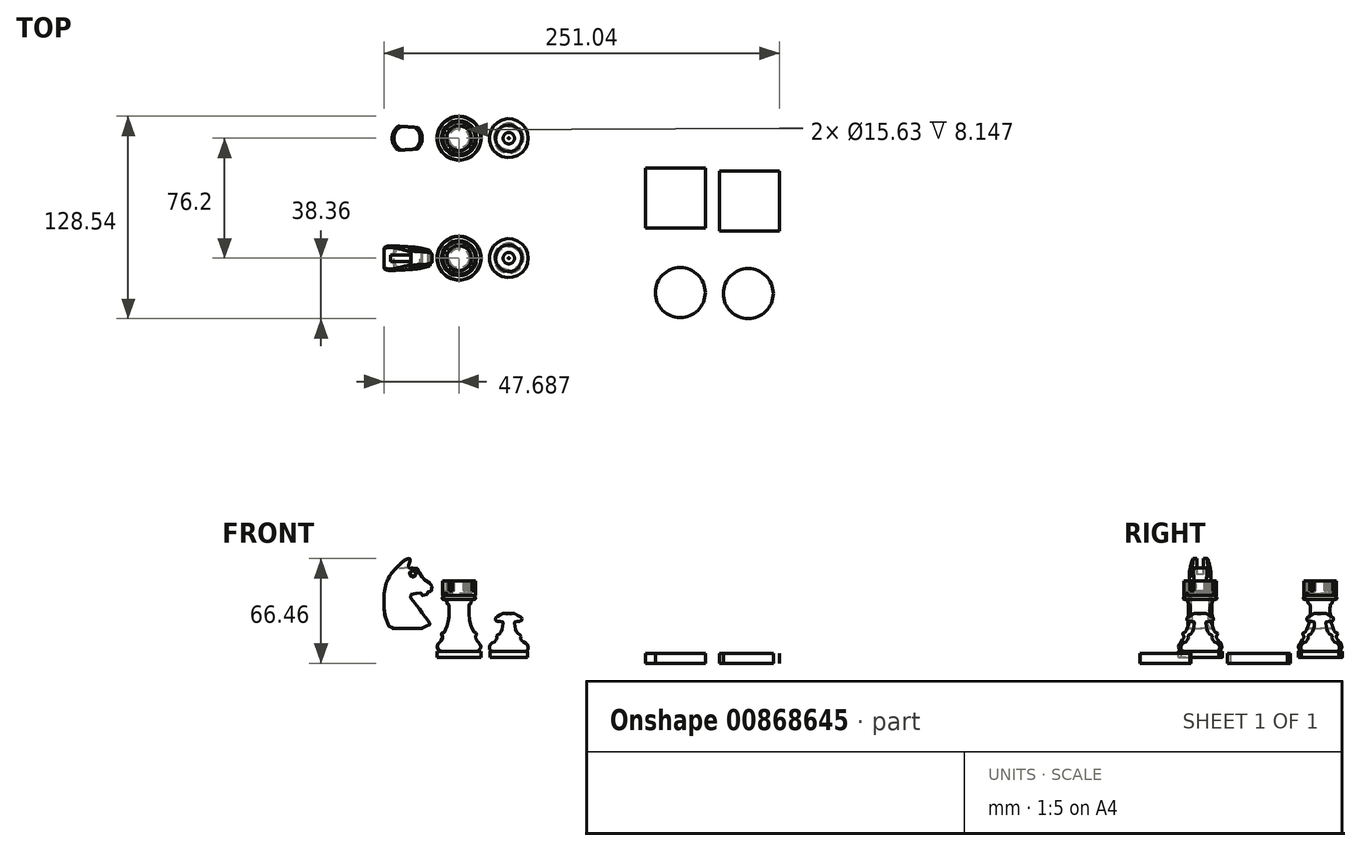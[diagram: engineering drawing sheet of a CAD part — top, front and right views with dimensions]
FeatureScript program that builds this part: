
annotation { "Feature Type Name" : "Feature", "Feature Type Description" : "" }
export const myFeature = defineFeature(function(context is Context, id is Id, definition is map)
    precondition{}
    {
        {
            var Q0;
            Q0=qCreatedBy(makeId("Front.planeOp"),FACE);
            var sketch = newSketch(context, id + "F0", { "sketchPlane" : qUnion([Q0])});
            skLineSegment(sketch, "E0", {"start": v(-199.85, 3.64) * mm, "end": v(-199.85, 7.41) * mm});
            skLineSegment(sketch, "E1", {"start": v(-183.09, 86.79) * mm, "end": v(-183.09, 3.64) * mm});
            skLineSegment(sketch, "E2", {"start": v(-183.09, 3.64) * mm, "end": v(-199.85, 3.64) * mm});
            skLineSegment(sketch, "E3", {"start": v(-199.85, 7.41) * mm, "end": v(-195.88, 7.41) * mm});
            skPoint(sketch, "E4.4.internal.snap0", {"position": v(-197.87, 7.41) * mm});
            skFitSpline(sketch, "E4", {"points": [v(-195.88, 7.41) * mm, v(-197.87, 8.5) * mm, v(-198.95, 10.23) * mm, v(-198.85, 12.89) * mm, v(-197.87, 14.53) * mm, v(-195.76, 16.55) * mm, v(-194.6, 17.92) * mm, v(-194.17, 19.06) * mm, v(-194.57, 20.66) * mm, v(-195.5, 21.71) * mm, v(-195.83, 22.33) * mm, v(-194.7, 22.77) * mm, v(-193.31, 23.31) * mm, v(-192.26, 24.37) * mm, v(-191.14, 25.8) * mm, v(-190.14, 27.4) * mm, v(-189.44, 29.17) * mm, v(-188.91, 31.11) * mm, v(-188.45, 33.14) * mm, v(-188.36, 34.84) * mm, v(-188.35, 36.72) * mm, v(-188.45, 38.4) * mm, v(-188.53, 39.6) * mm, v(-189, 41) * mm, v(-191.73, 41.08) * mm, v(-193.46, 41.44) * mm, v(-194.71, 42.76) * mm, v(-194.2, 44.5) * mm, v(-192.95, 45.2) * mm, v(-191.37, 45.33) * mm, v(-192.24, 45.83) * mm, v(-191.95, 47.6) * mm, v(-190.17, 47.87) * mm, v(-190.03, 49.22) * mm, v(-191.11, 49.48) * mm, v(-191.39, 50.58) * mm, v(-189.6, 51.19) * mm], "startDerivative": vector(-104.08, 42.72) * mm, "endDerivative": vector(159.54, -26.59) * mm});
            skLineSegment(sketch, "E5", {"start": v(-185.2, 71.42) * mm, "end": v(-188.29, 73.11) * mm});
            skLineSegment(sketch, "E6", {"start": v(-188.29, 73.11) * mm, "end": v(-185.32, 75.1) * mm});
            skLineSegment(sketch, "E7", {"start": v(-185.32, 75.1) * mm, "end": v(-189.6, 75.1) * mm});
            skLineSegment(sketch, "E8", {"start": v(-189.6, 75.1) * mm, "end": v(-189.6, 81.24) * mm});
            skLineSegment(sketch, "E9", {"start": v(-189.6, 81.24) * mm, "end": v(-184.77, 81.24) * mm});
            skFitSpline(sketch, "E10", {"points": [v(-189.6, 51.19) * mm, v(-194.54, 65.85) * mm, v(-192.56, 67.9) * mm, v(-188.33, 68.71) * mm, v(-187.1, 69) * mm, v(-188.31, 70.17) * mm, v(-187.66, 71) * mm, v(-185.2, 71.42) * mm], "startDerivative": vector(-6.3, 14.3) * mm, "endDerivative": vector(19.07, 2.88) * mm});
            skPoint(sketch, "E11.2.internal.snap0", {"position": v(-187.18, 81.24) * mm});
            skPoint(sketch, "E11.3.internal.snap0", {"position": v(-187.18, 81.24) * mm});
            skFitSpline(sketch, "E11", {"points": [v(-184.77, 81.24) * mm, v(-186.5, 82.07) * mm, v(-187.18, 83.38) * mm, v(-187.18, 84.69) * mm, v(-186.15, 85.79) * mm, v(-184.77, 86.55) * mm, v(-183.09, 86.79) * mm], "startDerivative": vector(-10.63, 3.55) * mm, "endDerivative": vector(10.1, 0.69) * mm});
            skLineSegment(sketch, "E12", {"start": v(-162.47, 3.64) * mm, "end": v(-147.45, 3.64) * mm});
            skLineSegment(sketch, "E13", {"start": v(-147.45, 3.64) * mm, "end": v(-147.45, 73.04) * mm});
            skArc(sketch, "E14", {"start": v(-147.45, 73.04) * mm, "mid": v(-151.14, 70.8) * mm, "end": v(-148.43, 67.44) * mm});
            skArc(sketch, "E15", {"start": v(-148.43, 67.44) * mm, "mid": v(-152.95, 65.09) * mm, "end": v(-155.31, 60.57) * mm});
            skLineSegment(sketch, "E16", {"start": v(-162.47, 3.64) * mm, "end": v(-162.47, 7.42) * mm});
            skLineSegment(sketch, "E17", {"start": v(-162.47, 7.42) * mm, "end": v(-158.12, 7.42) * mm});
            skPoint(sketch, "E18.1.internal.snap0", {"position": v(-160.3, 7.42) * mm});
            skPoint(sketch, "E18.4.internal.snap0", {"position": v(-160.3, 7.42) * mm});
            skPoint(sketch, "E18.7.internal.snap0", {"position": v(-160.3, 7.42) * mm});
            skFitSpline(sketch, "E18", {"points": [v(-158.12, 7.42) * mm, v(-160.3, 8.25) * mm, v(-161.95, 10.36) * mm, v(-161.95, 13.37) * mm, v(-160.3, 16.08) * mm, v(-159.02, 17.75) * mm, v(-158.68, 20.43) * mm, v(-160.3, 22.38) * mm, v(-158.12, 23) * mm, v(-155.74, 25.18) * mm, v(-154.18, 28.37) * mm, v(-153.34, 32.28) * mm, v(-153.18, 35.56) * mm, v(-153.3, 38.31) * mm, v(-154.3, 40) * mm, v(-158.12, 40.69) * mm, v(-159.15, 41.5) * mm, v(-158.77, 43.64) * mm, v(-155.8, 44.28) * mm, v(-156.78, 44.74) * mm], "startDerivative": vector(-84.67, 31.47) * mm, "endDerivative": vector(-14.48, 19.3) * mm});
            skFitSpline(sketch, "E19", {"points": [v(-155.8, 44.28) * mm, v(-156.78, 44.74) * mm, v(-156.78, 46.4) * mm, v(-155.31, 46.86) * mm, v(-154.54, 47.02) * mm, v(-154.46, 47.67) * mm, v(-155.31, 48) * mm, v(-155.8, 48.59) * mm, v(-155.31, 49.3) * mm, v(-154.8, 49.4) * mm, v(-154.74, 50.75) * mm, v(-154.96, 53) * mm, v(-155.31, 54.38) * mm, v(-156.58, 56.29) * mm, v(-158.17, 57.83) * mm, v(-159.9, 58.84) * mm, v(-159.55, 60.57) * mm, v(-157.83, 61.78) * mm, v(-157.79, 60.57) * mm, v(-156.78, 59.8) * mm, v(-155.31, 60.57) * mm], "startDerivative": vector(25.67, -12.83) * mm, "endDerivative": vector(13.36, 18.62) * mm});
            skLineSegment(sketch, "E20", {"start": v(-113.8, 67.45) * mm, "end": v(-113.8, 3.64) * mm});
            skLineSegment(sketch, "E21", {"start": v(-113.8, 3.64) * mm, "end": v(-127.93, 3.64) * mm});
            skLineSegment(sketch, "E22", {"start": v(-127.93, 3.64) * mm, "end": v(-127.93, 7.42) * mm});
            skLineSegment(sketch, "E23", {"start": v(-127.93, 7.42) * mm, "end": v(-124.73, 7.42) * mm});
            skLineSegment(sketch, "E24", {"start": v(-203.2, 3.64) * mm, "end": v(0.2, 3.64) * mm, "construction": true});
            skLineSegment(sketch, "E25", {"start": v(-0.21, 7.42) * mm, "end": v(-203.2, 7.42) * mm, "construction": true});
            skPoint(sketch, "E26.orphan", {"position": v(-164.6, 7.42) * mm});
            skFitSpline(sketch, "E27", {"points": [v(-124.73, 7.42) * mm, v(-126, 7.93) * mm, v(-127.06, 8.77) * mm, v(-127.82, 10.15) * mm, v(-127.96, 11.35) * mm, v(-127.51, 12.72) * mm, v(-126.8, 13.65) * mm, v(-125.88, 14.3) * mm, v(-124.95, 14.88) * mm, v(-124.14, 15.63) * mm, v(-123.67, 16.5) * mm, v(-123.67, 17.98) * mm, v(-124.73, 19.52) * mm, v(-123.1, 20.19) * mm, v(-121.55, 21.43) * mm, v(-120.23, 23.7) * mm, v(-119.36, 25.7) * mm, v(-118.68, 28.19) * mm, v(-118.44, 30.53) * mm, v(-118.68, 33.54) * mm, v(-120.4, 33.98) * mm, v(-122.54, 34.42) * mm, v(-124, 35.4) * mm, v(-124.17, 36.4) * mm, v(-123.83, 37.34) * mm, v(-122.39, 38.09) * mm, v(-120.99, 38.5) * mm, v(-121.51, 39.23) * mm, v(-121.67, 40.1) * mm, v(-120.93, 40.57) * mm, v(-120.07, 40.83) * mm, v(-119.28, 41.3) * mm, v(-119.17, 42.67) * mm, v(-119.8, 43.04) * mm, v(-120.12, 43.62) * mm, v(-119.67, 44.06) * mm, v(-119.36, 44.12) * mm, v(-120.86, 45.59) * mm, v(-122.01, 47.27) * mm, v(-122.54, 48.85) * mm, v(-122.96, 50.74) * mm, v(-122.75, 52.74) * mm, v(-121.96, 55.36) * mm, v(-120.54, 57.83) * mm, v(-119.28, 59.3) * mm, v(-117.86, 60.62) * mm, v(-115.55, 62.25) * mm], "startDerivative": vector(-65.25, 19.9) * mm, "endDerivative": vector(68.19, 36.9) * mm});
            skArc(sketch, "E28", {"start": v(-113.8, 67.45) * mm, "mid": v(-116.75, 65.54) * mm, "end": v(-115.55, 62.25) * mm});
            skLineSegment(sketch, "E29", {"start": v(-108.32, 59.77) * mm, "end": v(-112.78, 53.82) * mm});
            skLineSegment(sketch, "E30", {"start": v(-112.78, 53.82) * mm, "end": v(-111.45, 52.82) * mm});
            skLineSegment(sketch, "E31", {"start": v(-111.45, 52.82) * mm, "end": v(-107.21, 58.47) * mm});
            skArc(sketch, "E32", {"start": v(-107.21, 58.47) * mm, "mid": v(-106.96, 59.81) * mm, "end": v(-108.32, 59.77) * mm});
            skLineSegment(sketch, "E33", {"start": v(-81.1, 22.23) * mm, "end": v(-81.1, 3.64) * mm});
            skLineSegment(sketch, "E34", {"start": v(-81.1, 3.64) * mm, "end": v(-94.38, 3.64) * mm});
            skLineSegment(sketch, "E35", {"start": v(-94.38, 3.64) * mm, "end": v(-94.38, 7.42) * mm});
            skLineSegment(sketch, "E36", {"start": v(-94.38, 7.42) * mm, "end": v(-90.56, 7.42) * mm});
            skFitSpline(sketch, "E37", {"points": [v(-90.56, 7.42) * mm, v(-92.55, 8.07) * mm, v(-93.98, 9.16) * mm, v(-94.56, 10.65) * mm, v(-94.5, 12.37) * mm, v(-93.76, 13.69) * mm, v(-92.27, 15) * mm, v(-91.12, 16.04) * mm, v(-89.92, 17.64) * mm, v(-89.74, 19.07) * mm, v(-90.56, 20.16) * mm, v(-91.58, 20.97) * mm, v(-91.7, 21.54) * mm, v(-90.56, 22.11) * mm, v(-89.46, 22.23) * mm], "startDerivative": vector(-24.3, 6.47) * mm, "endDerivative": vector(16.76, 0.42) * mm});
            skLineSegment(sketch, "E38", {"start": v(-89.46, 22.23) * mm, "end": v(-81.1, 22.23) * mm});
            skLineSegment(sketch, "E39", {"start": v(-81.1, 22.23) * mm, "end": v(-72, 22.23) * mm});
            skFitSpline(sketch, "E40", {"points": [v(-89.46, 22.23) * mm, v(-91.2, 22.91) * mm, v(-92.34, 23.3) * mm, v(-93.93, 26.73) * mm, v(-95.27, 31.07) * mm, v(-95.78, 40.69) * mm, v(-95.08, 48.01) * mm, v(-92.6, 54.7) * mm, v(-87.82, 60.76) * mm, v(-83.04, 65.15) * mm, v(-80.42, 66.43) * mm, v(-79.15, 66.1) * mm, v(-79.66, 63.5) * mm, v(-80.17, 60.82) * mm, v(-77.62, 60.46) * mm, v(-74.88, 60.37) * mm, v(-73.73, 58.4) * mm, v(-71.82, 55.02) * mm, v(-67.17, 51) * mm, v(-65.58, 50.05) * mm, v(-65.64, 46.42) * mm, v(-66.22, 45.53) * mm, v(-67.62, 46.04) * mm, v(-68.06, 45.97) * mm, v(-68.02, 45.56) * mm, v(-67.03, 45.16) * mm, v(-68.33, 43.99) * mm, v(-69.6, 43.13) * mm, v(-72.16, 43.4) * mm, v(-71.53, 44.4) * mm, v(-72.93, 44.62) * mm, v(-76, 44.21) * mm, v(-78.42, 43.72) * mm, v(-79.19, 43.63) * mm, v(-79.5, 42.68) * mm, v(-78.15, 40.74) * mm, v(-73.83, 35.2) * mm, v(-67.16, 26.15) * mm, v(-66.48, 24.84) * mm, v(-67.2, 24.2) * mm, v(-72, 22.23) * mm], "startDerivative": vector(-89.03, 42.06) * mm, "endDerivative": vector(-168.6, -65.06) * mm});
            skLineSegment(sketch, "E41", {"start": v(-48.1, 44.33) * mm, "end": v(-48.1, 3.64) * mm});
            skLineSegment(sketch, "E42", {"start": v(-48.1, 3.64) * mm, "end": v(-62.08, 3.64) * mm});
            skLineSegment(sketch, "E43", {"start": v(-62.08, 3.64) * mm, "end": v(-62.08, 7.42) * mm});
            skLineSegment(sketch, "E44", {"start": v(-62.08, 7.42) * mm, "end": v(-58.5, 7.42) * mm});
            skFitSpline(sketch, "E45", {"points": [v(-58.5, 7.42) * mm, v(-60.07, 7.9) * mm, v(-61.28, 8.85) * mm, v(-61.91, 10.22) * mm, v(-61.65, 11.69) * mm, v(-60.39, 13.37) * mm, v(-59.02, 15.05) * mm, v(-58.5, 16.84) * mm, v(-59.02, 18.26) * mm, v(-59.28, 18.94) * mm, v(-58.5, 19.41) * mm, v(-57.4, 20) * mm, v(-55.87, 23.62) * mm, v(-54.66, 28.14) * mm, v(-54.45, 36.13) * mm, v(-54.7, 37.6) * mm, v(-55.18, 37.7) * mm, v(-55.81, 38.12) * mm, v(-55.81, 39.07) * mm, v(-56.55, 40.07) * mm, v(-57.23, 40.44) * mm, v(-58.5, 40.65) * mm, v(-58.5, 42.07) * mm, v(-57.4, 42.49) * mm, v(-58.44, 43.17) * mm], "startDerivative": vector(-47.74, 11.1) * mm, "endDerivative": vector(-43.2, 43.2) * mm});
            skLineSegment(sketch, "E46", {"start": v(-58.44, 43.17) * mm, "end": v(-58.44, 52.47) * mm});
            skLineSegment(sketch, "E47", {"start": v(-58.44, 52.47) * mm, "end": v(-55.92, 52.47) * mm});
            skLineSegment(sketch, "E48", {"start": v(-55.92, 52.47) * mm, "end": v(-55.92, 44.33) * mm});
            skLineSegment(sketch, "E49", {"start": v(-55.92, 44.33) * mm, "end": v(-48.1, 44.33) * mm});
            skLineSegment(sketch, "E50", {"start": v(-16.51, 46.86) * mm, "end": v(-16.51, 3.64) * mm});
            skLineSegment(sketch, "E51", {"start": v(-28.54, 3.64) * mm, "end": v(-28.54, 7.42) * mm});
            skLineSegment(sketch, "E52", {"start": v(-28.54, 7.42) * mm, "end": v(-26.05, 7.42) * mm});
            skFitSpline(sketch, "E53", {"points": [v(-26.05, 7.42) * mm, v(-28.06, 8.02) * mm, v(-28.67, 8.98) * mm, v(-28.85, 10.67) * mm, v(-27.88, 12.4) * mm, v(-25.72, 13.71) * mm, v(-24.53, 14.77) * mm, v(-24, 16.37) * mm, v(-24.3, 17.6) * mm, v(-23.06, 18.44) * mm, v(-22, 19.33) * mm, v(-20.8, 21.5) * mm, v(-20.27, 24.06) * mm, v(-20.26, 26.22) * mm, v(-20.94, 26.53) * mm, v(-23.19, 26.71) * mm, v(-24.59, 27) * mm, v(-24.95, 28.67) * mm, v(-23.59, 29.76) * mm, v(-20.12, 31.82) * mm], "startDerivative": vector(-40.56, 0) * mm, "endDerivative": vector(53.61, 36) * mm});
            skArc(sketch, "E54", {"start": v(-16.51, 46.86) * mm, "mid": v(-24.38, 40.8) * mm, "end": v(-20.12, 31.82) * mm});
            skLineSegment(sketch, "E55", {"start": v(-28.54, 3.64) * mm, "end": v(-16.51, 3.64) * mm});
            skLineSegment(sketch, "E56", {"start": v(-185.32, 75.1) * mm, "end": v(-183.09, 75.1) * mm});
            skLineSegment(sketch, "E57", {"start": v(-184.77, 81.24) * mm, "end": v(-183.09, 81.24) * mm});
            skLineSegment(sketch, "E58.MirrorCS", {"start": v(-176.58, 81.24) * mm, "end": v(-181.4, 81.24) * mm});
            skLineSegment(sketch, "E59.MirrorCS", {"start": v(-181.4, 81.24) * mm, "end": v(-183.09, 81.24) * mm});
            skLineSegment(sketch, "E60.MirrorCS", {"start": v(-176.58, 75.1) * mm, "end": v(-176.58, 81.24) * mm});
            skLineSegment(sketch, "E61.MirrorCS", {"start": v(-180.85, 75.1) * mm, "end": v(-176.58, 75.1) * mm});
            skLineSegment(sketch, "E62.MirrorCS", {"start": v(-180.85, 75.1) * mm, "end": v(-183.09, 75.1) * mm});
            skLineSegment(sketch, "E63", {"start": v(-158.15, 61.76) * mm, "end": v(-159.98, 58.99) * mm});
            skFitSpline(sketch, "E64", {"points": [v(-77.62, 60.46) * mm, v(-81.58, 60.46) * mm, v(-86.12, 60.08) * mm, v(-88.95, 59.2) * mm, v(-91.47, 56.45) * mm], "startDerivative": vector(-28.5, -2.2) * mm, "endDerivative": vector(-9.14, -10.07) * mm});
            skArc(sketch, "E65", {"start": v(-78.9, 58.36) * mm, "mid": v(-76.13, 55.42) * mm, "end": v(-78.63, 58.6) * mm});
            skArc(sketch, "E66", {"start": v(-78.58, 58.1) * mm, "mid": v(-76.44, 55.7) * mm, "end": v(-78.35, 58.29) * mm});
            skLineSegment(sketch, "E67", {"start": v(-78.35, 58.29) * mm, "end": v(-78.63, 58.6) * mm});
            skLineSegment(sketch, "E68", {"start": v(-78.58, 58.1) * mm, "end": v(-78.9, 58.36) * mm});
            skSolve(sketch);
        }
        {
            var Q0;
            Q0=makeQuery(id+"F0.imprint","IMPRINT",FACE,{"disambiguationData":[TD([[makeQuery(id+"F0.imprint","IMPRINT",EDGE,{"derivedFrom":sQuery(id+"F0.wireOp",EDGE,"E0")}),-1.0]])]});
            var Q1;
            {var subQ0=sQuery(id+"F0.wireOp",EDGE,"E11");Q1=makeQuery(id+"F0.imprint","IMPRINT",FACE,{"disambiguationData":[TD([[makeQuery(id+"F0.imprint","IMPRINT",EDGE,{"derivedFrom":subQ0}),-1.0]])]});}
            var Q2;
            Q2=sQuery(id+"F0.wireOp",EDGE,"E1");
            revolve(context, id + "F1", {"surfaceOperationType" : NewSurfaceOperationType.NEW, "entities" : qUnion([Q0, Q1]), "axis" : qUnion([Q2]), "revolveType" : RevolveType.FULL});
        }
        {
            var Q0;
            Q0=makeQuery(id+"F0.imprint","IMPRINT",FACE,{"disambiguationData":[TD([[makeQuery(id+"F0.imprint","IMPRINT",EDGE,{"derivedFrom":sQuery(id+"F0.wireOp",EDGE,"E58.MirrorCS")}),1.0]])]});
            var Q1;
            Q1=makeQuery(id+"F0.imprint","IMPRINT",FACE,{"disambiguationData":[TD([[makeQuery(id+"F0.imprint","IMPRINT",EDGE,{"derivedFrom":sQuery(id+"F0.wireOp",EDGE,"E7")}),-1.0]])]});
            extrude(context, id + "F2", {"entities" : qUnion([Q0, Q1]), "endBound" : BoundingType.SYMMETRIC, "depth" : 4.32 * mm, "offsetDistance" : 25.4 * mm});
        }
        {
            var Q0;
            Q0=makeQuery(id+"F0.imprint","IMPRINT",FACE,{"disambiguationData":[TD([[makeQuery(id+"F0.imprint","IMPRINT",EDGE,{"derivedFrom":sQuery(id+"F0.wireOp",EDGE,"E12")}),1.0]])]});
            var Q1;
            {var subQ0=sQuery(id+"F0.wireOp",EDGE,"E63");Q1=makeQuery(id+"F0.imprint","IMPRINT",FACE,{"disambiguationData":[TD([[makeQuery(id+"F0.imprint","IMPRINT",EDGE,{"derivedFrom":subQ0}),-1.0]])]});}
            var Q2;
            Q2=sQuery(id+"F0.wireOp",EDGE,"E13");
            revolve(context, id + "F3", {"surfaceOperationType" : NewSurfaceOperationType.NEW, "entities" : qUnion([Q0, Q1]), "axis" : qUnion([Q2]), "revolveType" : RevolveType.FULL});
        }
        {
            var Q0;
            {var subQ0=sQuery(id+"F0.wireOp",EDGE,"E63");Q0=makeQuery(id+"F0.imprint","IMPRINT",FACE,{"disambiguationData":[TD([[makeQuery(id+"F0.imprint","IMPRINT",EDGE,{"derivedFrom":subQ0}),-1.0]])]});}
            extrude(context, id + "F4", {"entities" : qUnion([Q0]), "operationType" : NewBodyOperationType.REMOVE, "endBound" : BoundingType.SYMMETRIC, "oppositeDirection" : true, "depth" : 7.62 * mm, "offsetDistance" : 25.4 * mm});
        }
        {
            var Q0;
            Q0=makeQuery(id+"F0.imprint","IMPRINT",FACE,{"disambiguationData":[TD([[makeQuery(id+"F0.imprint","IMPRINT",EDGE,{"derivedFrom":sQuery(id+"F0.wireOp",EDGE,"E20")}),-1.0]])]});
            var Q1;
            Q1=sQuery(id+"F0.wireOp",EDGE,"E20");
            revolve(context, id + "F5", {"surfaceOperationType" : NewSurfaceOperationType.NEW, "entities" : qUnion([Q0]), "axis" : qUnion([Q1]), "revolveType" : RevolveType.FULL});
        }
        {
            var Q0;
            Q0=makeQuery(id+"F0.imprint","IMPRINT",FACE,{"disambiguationData":[TD([[makeQuery(id+"F0.imprint","IMPRINT",EDGE,{"derivedFrom":sQuery(id+"F0.wireOp",EDGE,"E29")}),1.0]])]});
            extrude(context, id + "F6", {"entities" : qUnion([Q0]), "operationType" : NewBodyOperationType.REMOVE, "endBound" : BoundingType.SYMMETRIC, "oppositeDirection" : true, "depth" : 25.4 * mm, "offsetDistance" : 25.4 * mm});
        }
        {
            var Q0;
            Q0=makeQuery(id+"F0.imprint","IMPRINT",FACE,{"disambiguationData":[TD([[makeQuery(id+"F0.imprint","IMPRINT",EDGE,{"derivedFrom":sQuery(id+"F0.wireOp",EDGE,"E33")}),-1.0]])]});
            var Q1;
            Q1=sQuery(id+"F0.wireOp",EDGE,"E33");
            revolve(context, id + "F7", {"surfaceOperationType" : NewSurfaceOperationType.NEW, "entities" : qUnion([Q0]), "axis" : qUnion([Q1]), "revolveType" : RevolveType.FULL});
        }
        {
            var Q0;
            Q0=makeQuery(id+"F0.imprint","IMPRINT",FACE,{"disambiguationData":[TD([[makeQuery(id+"F0.imprint","IMPRINT",EDGE,{"derivedFrom":sQuery(id+"F0.wireOp",EDGE,"E38")}),1.0]])]});
            var Q1;
            {var subQ0=sQuery(id+"F0.wireOp",EDGE,"E64");var subQ1=sQuery(id+"F0.wireOp",EDGE,"E40");var subQ2=makeQuery(id+"F0.imprint","INTERSECT",VERTEX,{"disambiguationData":[OD(1.0)],"derivedFrom":[subQ1,subQ0]});Q1=makeQuery(id+"F0.imprint","IMPRINT",FACE,{"disambiguationData":[TD([[makeQuery(id+"F0.imprint","IMPRINT",EDGE,{"disambiguationData":[TD([[subQ2,-1.0]])],"derivedFrom":subQ1}),-1.0]])]});}
            extrude(context, id + "F8", {"entities" : qUnion([Q0, Q1]), "endBound" : BoundingType.SYMMETRIC, "depth" : 16.5 * mm, "offsetDistance" : 25.4 * mm});
        }
        {
            var Q0;
            Q0=makeQuery(id+"F0.imprint","IMPRINT",FACE,{"disambiguationData":[TD([[makeQuery(id+"F0.imprint","IMPRINT",EDGE,{"derivedFrom":sQuery(id+"F0.wireOp",EDGE,"E65")}),1.0]])]});
            extrude(context, id + "F9", {"entities" : qUnion([Q0]), "operationType" : NewBodyOperationType.ADD, "endBound" : BoundingType.SYMMETRIC, "depth" : 8.9 * mm, "offsetDistance" : 25.4 * mm});
        }
        {
            var Q0;
            Q0=qCreatedBy(makeId("Top.planeOp"),FACE);
            cPlane(context, id + "F10", {"entities" : qUnion([Q0]), "cplaneType" : CPlaneType.OFFSET, "offset" : 68.58 * mm, "width" : 152.4 * mm, "height" : 152.4 * mm});
        }
        {
            var Q0;
            Q0=qCreatedBy(id+"F10.planeOp",FACE);
            var sketch = newSketch(context, id + "F11", { "sketchPlane" : qUnion([Q0])});
            skLineSegment(sketch, "E69", {"start": v(-96.93, 0) * mm, "end": v(-65.24, 0) * mm, "construction": true});
            skFitSpline(sketch, "E70", {"points": [v(-96.93, 0) * mm, v(-96.06, 4.1) * mm, v(-93.85, 5.9) * mm, v(-90.77, 6.5) * mm, v(-83.35, 5.08) * mm, v(-77.27, 3.96) * mm, v(-72.02, 3.38) * mm, v(-68.06, 2.89) * mm, v(-65.82, 1.67) * mm, v(-65.24, 0) * mm], "startDerivative": vector(5.1, 33.54) * mm, "endDerivative": vector(-0.64, -25.5) * mm});
            skFitSpline(sketch, "E71.MirrorCS", {"points": [v(-96.93, 0) * mm, v(-96.06, -4.1) * mm, v(-93.85, -5.9) * mm, v(-90.77, -6.5) * mm, v(-83.35, -5.08) * mm, v(-77.27, -3.96) * mm, v(-72.02, -3.38) * mm, v(-68.06, -2.89) * mm, v(-65.82, -1.67) * mm, v(-65.24, 0) * mm], "startDerivative": vector(5.1, -33.54) * mm, "endDerivative": vector(-0.64, 25.5) * mm});
            skSolve(sketch);
        }
        {
            var Q0;
            Q0=qCreatedBy(makeId("Top.planeOp"),FACE);
            cPlane(context, id + "F12", {"entities" : qUnion([Q0]), "cplaneType" : CPlaneType.OFFSET, "offset" : 22.1 * mm, "width" : 152.4 * mm, "height" : 152.4 * mm});
        }
        {
            var Q0;
            Q0=qCreatedBy(id+"F12.planeOp",FACE);
            var sketch = newSketch(context, id + "F13", { "sketchPlane" : qUnion([Q0])});
            skLineSegment(sketch, "E72.0", {"start": v(-96.93, 0) * mm, "end": v(-65.24, 0) * mm, "construction": true});
            skFitSpline(sketch, "E73", {"points": [v(-97.18, 0) * mm, v(-96.91, -4.02) * mm, v(-95.8, -7.1) * mm, v(-91.1, -7.8) * mm, v(-82.32, -7.36) * mm, v(-73.94, -6.64) * mm, v(-67.8, -5.37) * mm, v(-64.85, -4.29) * mm, v(-63.2, -2.29) * mm, v(-63.11, 0) * mm], "startDerivative": vector(-0.16, -37.52) * mm, "endDerivative": vector(4.17, 26.23) * mm});
            skFitSpline(sketch, "E74.MirrorCS", {"points": [v(-97.18, 0) * mm, v(-96.91, 4.02) * mm, v(-95.8, 7.1) * mm, v(-91.1, 7.8) * mm, v(-82.32, 7.36) * mm, v(-73.94, 6.64) * mm, v(-67.8, 5.37) * mm, v(-64.85, 4.29) * mm, v(-63.2, 2.29) * mm, v(-63.11, 0) * mm], "startDerivative": vector(-0.16, 37.52) * mm, "endDerivative": vector(4.17, -26.23) * mm});
            skSolve(sketch);
        }
        {
            var Q1;
            Q1=makeQuery(id+"F13.imprint","IMPRINT",FACE,{"disambiguationData":[TD([[makeQuery(id+"F13.imprint","IMPRINT",EDGE,{"derivedFrom":sQuery(id+"F13.wireOp",EDGE,"E73")}),1.0]])]});
            var Q2;
            Q2=makeQuery(id+"F11.imprint","IMPRINT",FACE,{"disambiguationData":[TD([[makeQuery(id+"F11.imprint","IMPRINT",EDGE,{"derivedFrom":sQuery(id+"F11.wireOp",EDGE,"E70")}),-1.0]])]});
            loft(context, id + "F14", {"operationType" : NewBodyOperationType.INTERSECT, "sheetProfilesArray" : [{ "sheetProfileEntities" : qUnion([Q1]) }, { "sheetProfileEntities" : qUnion([Q2]) }]});
        }
        {
            var Q0;
            {var subQ0=sQuery(id+"F0.wireOp",EDGE,"E64");var subQ1=sQuery(id+"F0.wireOp",EDGE,"E40");var subQ2=makeQuery(id+"F0.imprint","INTERSECT",VERTEX,{"disambiguationData":[OD(1.0)],"derivedFrom":[subQ1,subQ0]});Q0=makeQuery(id+"F0.imprint","IMPRINT",FACE,{"disambiguationData":[TD([[makeQuery(id+"F0.imprint","IMPRINT",EDGE,{"disambiguationData":[TD([[subQ2,-1.0]])],"derivedFrom":subQ1}),-1.0]])]});}
            extrude(context, id + "F15", {"entities" : qUnion([Q0]), "operationType" : NewBodyOperationType.REMOVE, "endBound" : BoundingType.SYMMETRIC, "oppositeDirection" : true, "depth" : 4.32 * mm, "offsetDistance" : 25.4 * mm});
        }
        {
            var Q0;
            Q0=makeQuery(id+"F0.imprint","IMPRINT",FACE,{"disambiguationData":[TD([[makeQuery(id+"F0.imprint","IMPRINT",EDGE,{"derivedFrom":sQuery(id+"F0.wireOp",EDGE,"E41")}),-1.0]])]});
            var Q1;
            Q1=sQuery(id+"F0.wireOp",EDGE,"E41");
            revolve(context, id + "F16", {"surfaceOperationType" : NewSurfaceOperationType.NEW, "entities" : qUnion([Q0]), "axis" : qUnion([Q1]), "revolveType" : RevolveType.FULL});
        }
        {
            var Q0;
            Q0=makeQuery(id+"F16.opRevolve","SWEPT_FACE",FACE,{"disambiguationData":[OSD([sQuery(id+"F0.wireOp",EDGE,"E47")])]});
            var sketch = newSketch(context, id + "F17", { "sketchPlane" : qUnion([Q0])});
            skCircle(sketch, "E75.0", {"center": v(-48.1, 0) * mm, "radius": 7.82 * mm});
            skCircle(sketch, "E76.0", {"center": v(-48.1, 0) * mm, "radius": 10.34 * mm});
            skLineSegment(sketch, "E77", {"start": v(-42.1, -5) * mm, "end": v(-40.01, -6.44) * mm});
            skLineSegment(sketch, "E78", {"start": v(-40.8, -2.8) * mm, "end": v(-38.59, -4.04) * mm});
            skLineSegment(sketch, "E79.1.0", {"start": v(-45.3, 7.3) * mm, "end": v(-44.07, 9.52) * mm});
            skLineSegment(sketch, "E79.1.1", {"start": v(-43.11, 6.01) * mm, "end": v(-41.67, 8.09) * mm});
            skLineSegment(sketch, "E79.2.0", {"start": v(-55.4, 2.8) * mm, "end": v(-57.62, 4.04) * mm});
            skLineSegment(sketch, "E79.2.1", {"start": v(-54.12, 5) * mm, "end": v(-56.2, 6.44) * mm});
            skLineSegment(sketch, "E79.3.0", {"start": v(-50.9, -7.3) * mm, "end": v(-52.14, -9.52) * mm});
            skLineSegment(sketch, "E79.3.1", {"start": v(-53.1, -6.01) * mm, "end": v(-54.54, -8.09) * mm});
            skSolve(sketch);
        }
        {
            var Q0;
            {var subQ0=sQuery(id+"F17.wireOp",EDGE,"E77");Q0=makeQuery(id+"F17.imprint","IMPRINT",FACE,{"disambiguationData":[TD([[makeQuery(id+"F17.imprint","IMPRINT",EDGE,{"derivedFrom":subQ0}),1.0]])]});}
            var Q1;
            {var subQ0=sQuery(id+"F17.wireOp",EDGE,"E79.3.0");Q1=makeQuery(id+"F17.imprint","IMPRINT",FACE,{"disambiguationData":[TD([[makeQuery(id+"F17.imprint","IMPRINT",EDGE,{"derivedFrom":subQ0}),-1.0]])]});}
            var Q2;
            {var subQ0=sQuery(id+"F17.wireOp",EDGE,"E79.2.0");Q2=makeQuery(id+"F17.imprint","IMPRINT",FACE,{"disambiguationData":[TD([[makeQuery(id+"F17.imprint","IMPRINT",EDGE,{"derivedFrom":subQ0}),-1.0]])]});}
            var Q3;
            {var subQ0=sQuery(id+"F17.wireOp",EDGE,"E79.1.0");Q3=makeQuery(id+"F17.imprint","IMPRINT",FACE,{"disambiguationData":[TD([[makeQuery(id+"F17.imprint","IMPRINT",EDGE,{"derivedFrom":subQ0}),-1.0]])]});}
            extrude(context, id + "F18", {"entities" : qUnion([Q0, Q1, Q2, Q3]), "operationType" : NewBodyOperationType.REMOVE, "oppositeDirection" : true, "depth" : 6.35 * mm, "offsetDistance" : 25.4 * mm});
        }
        {
            var Q0;
            Q0=makeQuery(id+"F0.imprint","IMPRINT",FACE,{"disambiguationData":[TD([[makeQuery(id+"F0.imprint","IMPRINT",EDGE,{"derivedFrom":sQuery(id+"F0.wireOp",EDGE,"E50")}),-1.0]])]});
            var Q1;
            Q1=sQuery(id+"F0.wireOp",EDGE,"E50");
            revolve(context, id + "F19", {"surfaceOperationType" : NewSurfaceOperationType.NEW, "entities" : qUnion([Q0]), "axis" : qUnion([Q1]), "revolveType" : RevolveType.FULL});
        }
        {
            var Q0;
            Q0=makeQuery(id+"F1.opRevolve","SWEPT_BODY",BODY,{"disambiguationData":[OSD([sQuery(id+"F0.wireOp",EDGE,"E0"),sQuery(id+"F0.wireOp",EDGE,"E1"),sQuery(id+"F0.wireOp",EDGE,"E2"),sQuery(id+"F0.wireOp",EDGE,"E3"),sQuery(id+"F0.wireOp",EDGE,"E4"),sQuery(id+"F0.wireOp",EDGE,"E5"),sQuery(id+"F0.wireOp",EDGE,"E6"),sQuery(id+"F0.wireOp",EDGE,"E10"),sQuery(id+"F0.wireOp",EDGE,"E56")])]});
            var Q1;
            Q1=makeQuery(id+"F3.opRevolve","SWEPT_BODY",BODY,{"disambiguationData":[OSD([sQuery(id+"F0.wireOp",EDGE,"E12"),sQuery(id+"F0.wireOp",EDGE,"E13"),sQuery(id+"F0.wireOp",EDGE,"E14"),sQuery(id+"F0.wireOp",EDGE,"E15"),sQuery(id+"F0.wireOp",EDGE,"E16"),sQuery(id+"F0.wireOp",EDGE,"E17"),sQuery(id+"F0.wireOp",EDGE,"E18"),sQuery(id+"F0.wireOp",EDGE,"E19")])]});
            var Q2;
            Q2=makeQuery(id+"F5.opRevolve","SWEPT_BODY",BODY,{"disambiguationData":[OSD([sQuery(id+"F0.wireOp",EDGE,"E20"),sQuery(id+"F0.wireOp",EDGE,"E21"),sQuery(id+"F0.wireOp",EDGE,"E22"),sQuery(id+"F0.wireOp",EDGE,"E23"),sQuery(id+"F0.wireOp",EDGE,"E27"),sQuery(id+"F0.wireOp",EDGE,"E28")])]});
            var Q3;
            Q3=makeQuery(id+"F7.opRevolve","SWEPT_BODY",BODY,{"disambiguationData":[OSD([sQuery(id+"F0.wireOp",EDGE,"E33"),sQuery(id+"F0.wireOp",EDGE,"E34"),sQuery(id+"F0.wireOp",EDGE,"E35"),sQuery(id+"F0.wireOp",EDGE,"E36"),sQuery(id+"F0.wireOp",EDGE,"E37"),sQuery(id+"F0.wireOp",EDGE,"E38")])]});
            var Q4;
            Q4=makeQuery(id+"F16.opRevolve","SWEPT_BODY",BODY,{"disambiguationData":[OSD([sQuery(id+"F0.wireOp",EDGE,"E41"),sQuery(id+"F0.wireOp",EDGE,"E42"),sQuery(id+"F0.wireOp",EDGE,"E43"),sQuery(id+"F0.wireOp",EDGE,"E44"),sQuery(id+"F0.wireOp",EDGE,"E45"),sQuery(id+"F0.wireOp",EDGE,"E46"),sQuery(id+"F0.wireOp",EDGE,"E47"),sQuery(id+"F0.wireOp",EDGE,"E48"),sQuery(id+"F0.wireOp",EDGE,"E49")])]});
            var Q5;
            Q5=makeQuery(id+"F19.opRevolve","SWEPT_BODY",BODY,{"disambiguationData":[OSD([sQuery(id+"F0.wireOp",EDGE,"E50"),sQuery(id+"F0.wireOp",EDGE,"E51"),sQuery(id+"F0.wireOp",EDGE,"E52"),sQuery(id+"F0.wireOp",EDGE,"E53"),sQuery(id+"F0.wireOp",EDGE,"E54"),sQuery(id+"F0.wireOp",EDGE,"E55")])]});
            transform(context, id + "F20", {"entities" : qUnion([Q0, Q1, Q2, Q3, Q4, Q5]), "transformType" : TransformType.TRANSLATION_3D, "dx" : 0 * mm, "dy" : 76.2 * mm, "dz" : 0 * mm, "makeCopy" : true});
        }
        {
            var Q0;
            Q0=qCreatedBy(makeId("Top.planeOp"),FACE);
            var sketch = newSketch(context, id + "F21", { "sketchPlane" : qUnion([Q0])});
            skLineSegment(sketch, "E80.bottom", {"start": v(70.17, 19.13) * mm, "end": v(108.27, 19.13) * mm});
            skLineSegment(sketch, "E80.top", {"start": v(70.17, 57.23) * mm, "end": v(108.27, 57.23) * mm});
            skLineSegment(sketch, "E80.left", {"start": v(70.17, 19.13) * mm, "end": v(70.17, 57.23) * mm});
            skLineSegment(sketch, "E80.right", {"start": v(108.27, 19.13) * mm, "end": v(108.27, 57.23) * mm});
            skLineSegment(sketch, "E81.bottom", {"start": v(117.15, 55.48) * mm, "end": v(155.25, 55.48) * mm});
            skLineSegment(sketch, "E81.top", {"start": v(117.15, 17.38) * mm, "end": v(155.25, 17.38) * mm});
            skLineSegment(sketch, "E81.left", {"start": v(117.15, 55.48) * mm, "end": v(117.15, 17.38) * mm});
            skLineSegment(sketch, "E81.right", {"start": v(155.25, 55.48) * mm, "end": v(155.25, 17.38) * mm});
            skCircle(sketch, "E82", {"center": v(92.4, -21.87) * mm, "radius": 15.88 * mm});
            skCircle(sketch, "E83", {"center": v(135.57, -22.49) * mm, "radius": 15.88 * mm});
            skSolve(sketch);
        }
        {
            var Q0;
            Q0=makeQuery(id+"F21.imprint","IMPRINT",FACE,{"disambiguationData":[TD([[makeQuery(id+"F21.imprint","IMPRINT",EDGE,{"derivedFrom":sQuery(id+"F21.wireOp",EDGE,"E80.bottom")}),1.0]])]});
            var Q1;
            Q1=makeQuery(id+"F21.imprint","IMPRINT",FACE,{"disambiguationData":[TD([[makeQuery(id+"F21.imprint","IMPRINT",EDGE,{"derivedFrom":sQuery(id+"F21.wireOp",EDGE,"E81.bottom")}),-1.0]])]});
            var Q2;
            Q2=makeQuery(id+"F21.imprint","IMPRINT",FACE,{"disambiguationData":[TD([[makeQuery(id+"F21.imprint","IMPRINT",EDGE,{"derivedFrom":sQuery(id+"F21.wireOp",EDGE,"E82")}),1.0]])]});
            var Q3;
            Q3=makeQuery(id+"F21.imprint","IMPRINT",FACE,{"disambiguationData":[TD([[makeQuery(id+"F21.imprint","IMPRINT",EDGE,{"derivedFrom":sQuery(id+"F21.wireOp",EDGE,"E83")}),1.0]])]});
            extrude(context, id + "F22", {"entities" : qUnion([Q0, Q1, Q2, Q3]), "depth" : 6.35 * mm, "offsetDistance" : 25.4 * mm});
        }
    });
